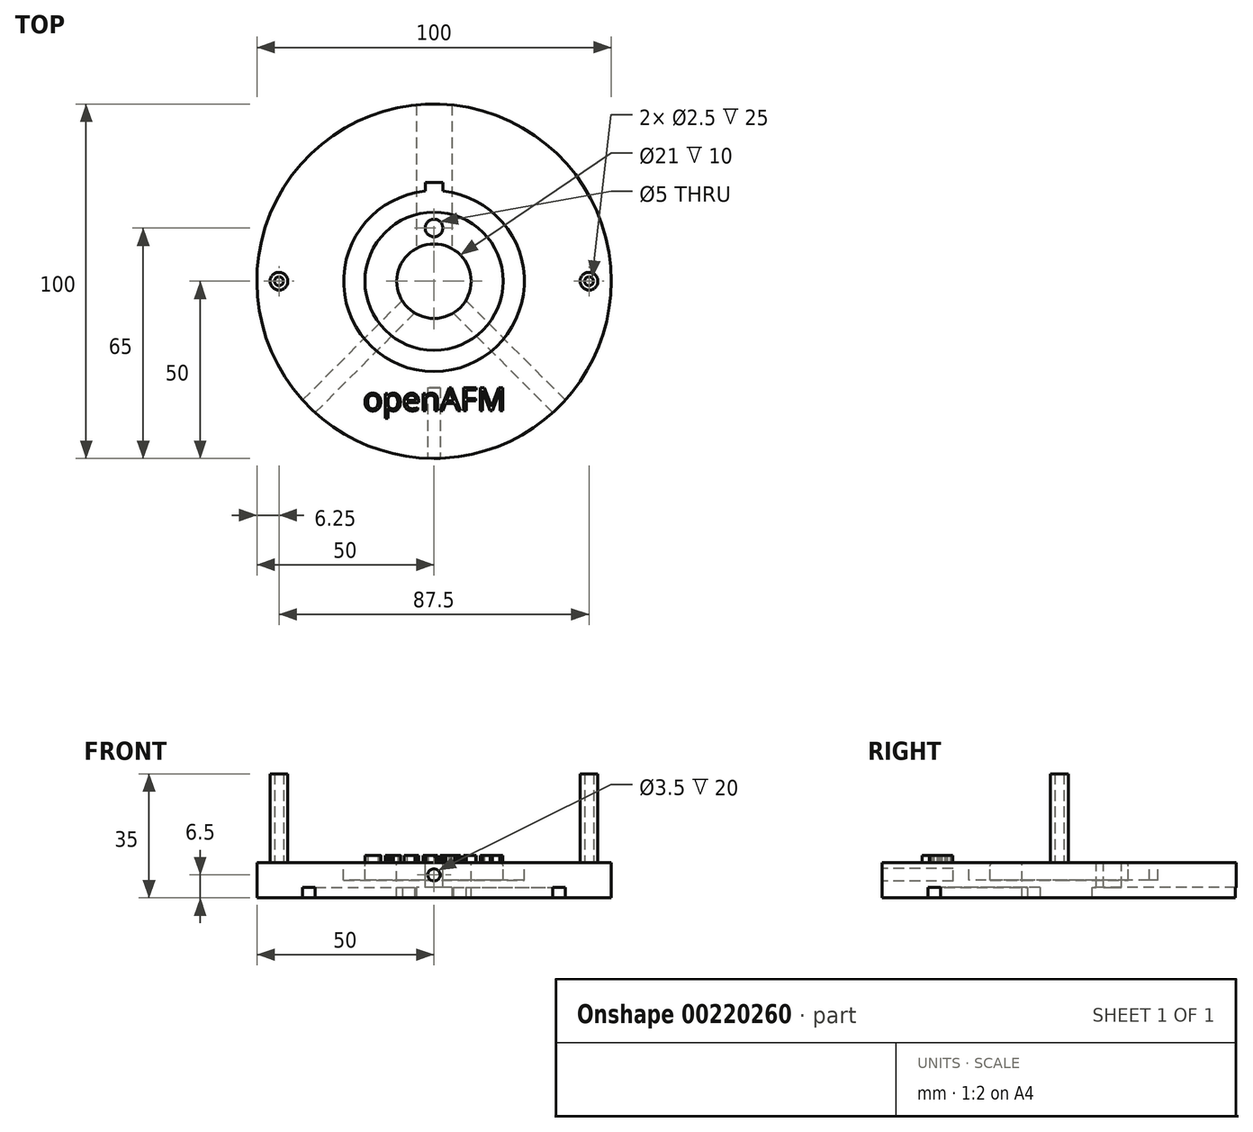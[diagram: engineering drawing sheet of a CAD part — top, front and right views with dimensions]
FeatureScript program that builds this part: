
annotation { "Feature Type Name" : "Feature", "Feature Type Description" : "" }
export const myFeature = defineFeature(function(context is Context, id is Id, definition is map)
    precondition{}
    {
        {
            var Q0;
            Q0=qCreatedBy(makeId("Top.planeOp"),FACE);
            var sketch = newSketch(context, id + "F0", { "sketchPlane" : qUnion([Q0])});
            skCircle(sketch, "E0", {"center": v(0, 0) * mm, "radius": 50 * mm});
            skSolve(sketch);
        }
        {
            var Q0;
            Q0=makeQuery(id+"F0.imprint","IMPRINT",FACE,{"disambiguationData":[TD([[makeQuery(id+"F0.imprint","IMPRINT",EDGE,{"derivedFrom":sQuery(id+"F0.wireOp",EDGE,"E0")}),1.0]])]});
            extrude(context, id + "F1", {"entities" : qUnion([Q0]), "depth" : 10 * mm});
        }
        {
            var Q0;
            Q0=makeQuery(id+"F1.opExtrude","CAP_FACE",FACE,{"disambiguationData":[OSD([sQuery(id+"F0.wireOp",EDGE,"E0")])],"isStart":false});
            var sketch = newSketch(context, id + "F2", { "sketchPlane" : qUnion([Q0])});
            skCircle(sketch, "E1", {"center": v(0, 0) * mm, "radius": 10.5 * mm});
            skSolve(sketch);
        }
        {
            var Q0;
            Q0=makeQuery(id+"F2.imprint","IMPRINT",FACE,{"disambiguationData":[TD([[makeQuery(id+"F2.imprint","IMPRINT",EDGE,{"derivedFrom":sQuery(id+"F2.wireOp",EDGE,"E1")}),1.0]])]});
            extrude(context, id + "F3", {"entities" : qUnion([Q0]), "operationType" : NewBodyOperationType.REMOVE, "oppositeDirection" : true, "depth" : 10 * mm});
        }
        {
            var Q0;
            Q0=makeQuery(id+"F1.opExtrude","CAP_FACE",FACE,{"disambiguationData":[OSD([sQuery(id+"F0.wireOp",EDGE,"E0")])],"isStart":true});
            var sketch = newSketch(context, id + "F4", { "sketchPlane" : qUnion([Q0])});
            skLineSegment(sketch, "E2", {"start": v(0, 0) * mm, "end": v(50, 0) * mm, "construction": true});
            skLineSegment(sketch, "E3", {"start": v(0, 0) * mm, "end": v(0, 50) * mm, "construction": true});
            skLineSegment(sketch, "E4", {"start": v(0, 0) * mm, "end": v(-50, 0) * mm, "construction": true});
            skLineSegment(sketch, "E5", {"start": v(0, 0) * mm, "end": v(0, -50) * mm, "construction": true});
            skLineSegment(sketch, "E6", {"start": v(0, 0) * mm, "end": v(-35.36, 35.36) * mm, "construction": true});
            skLineSegment(sketch, "E7", {"start": v(0, 0) * mm, "end": v(35.36, -35.36) * mm, "construction": true});
            skLineSegment(sketch, "E8", {"start": v(0, 0) * mm, "end": v(35.36, 35.36) * mm, "construction": true});
            skLineSegment(sketch, "E9", {"start": v(0, 0) * mm, "end": v(-35.36, -35.36) * mm, "construction": true});
            skLineSegment(sketch, "E10", {"start": v(-37.08, 33.54) * mm, "end": v(-8.98, 5.44) * mm});
            skLineSegment(sketch, "E11", {"start": v(-33.54, 37.08) * mm, "end": v(-5.44, 8.98) * mm});
            skArc(sketch, "E12", {"start": v(-8.98, -5.44) * mm, "mid": v(-7.42, -7.42) * mm, "end": v(-5.44, -8.98) * mm});
            skLineSegment(sketch, "E13.trimOffspring", {"start": v(5.44, -8.98) * mm, "end": v(33.54, -37.08) * mm});
            skLineSegment(sketch, "E14.trimOffspring", {"start": v(8.98, -5.44) * mm, "end": v(37.08, -33.54) * mm});
            skArc(sketch, "E15", {"start": v(-37.08, -33.54) * mm, "mid": v(-35.36, -35.36) * mm, "end": v(-33.54, -37.08) * mm});
            skLineSegment(sketch, "E16", {"start": v(-37.08, -33.54) * mm, "end": v(-8.98, -5.44) * mm});
            skLineSegment(sketch, "E17", {"start": v(-33.54, -37.08) * mm, "end": v(-5.44, -8.98) * mm});
            skLineSegment(sketch, "E18.trimOffspring", {"start": v(5.44, 8.98) * mm, "end": v(33.54, 37.08) * mm});
            skLineSegment(sketch, "E19.trimOffspring", {"start": v(8.98, 5.44) * mm, "end": v(37.08, 33.54) * mm});
            skArc(sketch, "E20.trimOffspring", {"start": v(-33.54, 37.08) * mm, "mid": v(-35.36, 35.36) * mm, "end": v(-37.08, 33.54) * mm});
            skArc(sketch, "E21.trimOffspring", {"start": v(37.08, 33.54) * mm, "mid": v(35.36, 35.36) * mm, "end": v(33.54, 37.08) * mm});
            skArc(sketch, "E22.trimOffspring", {"start": v(33.54, -37.08) * mm, "mid": v(35.36, -35.36) * mm, "end": v(37.08, -33.54) * mm});
            skArc(sketch, "E23.trimOffspring", {"start": v(-5.44, 8.98) * mm, "mid": v(-7.42, 7.42) * mm, "end": v(-8.98, 5.44) * mm});
            skArc(sketch, "E24.trimOffspring", {"start": v(8.98, 5.44) * mm, "mid": v(7.42, 7.42) * mm, "end": v(5.44, 8.98) * mm});
            skArc(sketch, "E25.trimOffspring", {"start": v(5.44, -8.98) * mm, "mid": v(7.42, -7.42) * mm, "end": v(8.98, -5.44) * mm});
            skLineSegment(sketch, "E26", {"start": v(-2.5, 10.2) * mm, "end": v(-2.5, 49.94) * mm});
            skLineSegment(sketch, "E27", {"start": v(2.5, 10.2) * mm, "end": v(2.5, 49.94) * mm});
            skLineSegment(sketch, "E28", {"start": v(2.5, 49.94) * mm, "end": v(2.93, 49.2) * mm});
            skArc(sketch, "E29", {"start": v(-2.5, 10.2) * mm, "mid": v(0, 10.5) * mm, "end": v(2.5, 10.2) * mm});
            skArc(sketch, "E30", {"start": v(-2.5, 49.94) * mm, "mid": v(0, 50) * mm, "end": v(2.5, 49.94) * mm});
            skSolve(sketch);
        }
        {
            var Q0;
            Q0=makeQuery(id+"F4.imprint","IMPRINT",FACE,{"disambiguationData":[TD([[makeQuery(id+"F4.imprint","IMPRINT",EDGE,{"derivedFrom":sQuery(id+"F4.wireOp",EDGE,"E10")}),1.0]])]});
            var Q1;
            Q1=makeQuery(id+"F4.imprint","IMPRINT",FACE,{"disambiguationData":[TD([[makeQuery(id+"F4.imprint","IMPRINT",EDGE,{"derivedFrom":sQuery(id+"F4.wireOp",EDGE,"E18.trimOffspring")}),-1.0]])]});
            extrude(context, id + "F5", {"entities" : qUnion([Q0, Q1]), "operationType" : NewBodyOperationType.REMOVE, "oppositeDirection" : true, "depth" : 3 * mm});
        }
        {
            var Q0;
            Q0=makeQuery(id+"F1.opExtrude","CAP_FACE",FACE,{"disambiguationData":[OSD([sQuery(id+"F0.wireOp",EDGE,"E0")])],"isStart":false});
            var sketch = newSketch(context, id + "F6", { "sketchPlane" : qUnion([Q0])});
            skCircle(sketch, "E31", {"center": v(0, 0) * mm, "radius": 19.5 * mm});
            skCircle(sketch, "E32", {"center": v(0, 0) * mm, "radius": 25.5 * mm});
            skSolve(sketch);
        }
        {
            var Q0;
            Q0=makeQuery(id+"F6.imprint","IMPRINT",FACE,{"disambiguationData":[TD([[makeQuery(id+"F6.imprint","IMPRINT",EDGE,{"derivedFrom":sQuery(id+"F6.wireOp",EDGE,"E31")}),-1.0]])]});
            extrude(context, id + "F7", {"entities" : qUnion([Q0]), "operationType" : NewBodyOperationType.REMOVE, "oppositeDirection" : true, "depth" : 5 * mm});
        }
        {
            var Q0;
            {var subQ0=sQuery(id+"F0.wireOp",EDGE,"E0");Q0=makeQuery(id+"F7.boolean.opBoolean","SPLIT",FACE,{"disambiguationData":[TD([makeQuery(id+"F1.opExtrude","SWEPT_FACE",FACE,{"disambiguationData":[OSD([subQ0])]})])],"derivedFrom":makeQuery(id+"F1.opExtrude","CAP_FACE",FACE,{"disambiguationData":[OSD([subQ0])],"isStart":false})});}
            var sketch = newSketch(context, id + "F8", { "sketchPlane" : qUnion([Q0])});
            skCircle(sketch, "E33", {"center": v(-43.75, 0) * mm, "radius": 2.5 * mm});
            skCircle(sketch, "E34", {"center": v(-43.75, 0) * mm, "radius": 1.25 * mm});
            skCircle(sketch, "E35", {"center": v(43.75, 0) * mm, "radius": 2.5 * mm});
            skCircle(sketch, "E36", {"center": v(43.75, 0) * mm, "radius": 1.25 * mm});
            skSolve(sketch);
        }
        {
            var Q0;
            Q0=qSketchRegion(id+"F8",true);
            extrude(context, id + "F9", {"entities" : qUnion([Q0]), "operationType" : NewBodyOperationType.ADD, "depth" : 25 * mm});
        }
        {
            var Q0;
            Q0=makeQuery(id+"F7.boolean.opBoolean","COPY",EDGE,{"derivedFrom":makeQuery(id+"F7.opExtrude","CAP_EDGE",EDGE,{"disambiguationData":[OSD([sQuery(id+"F6.wireOp",EDGE,"E31")])],"isStart":true})});
            var Q1;
            Q1=makeQuery(id+"F7.boolean.opBoolean","COPY",EDGE,{"derivedFrom":makeQuery(id+"F7.opExtrude","CAP_EDGE",EDGE,{"disambiguationData":[OSD([sQuery(id+"F6.wireOp",EDGE,"E32")])],"isStart":true})});
            fillet(context, id + "F10", {"entities" : qUnion([Q0, Q1]), "radius" : 1 * mm, "tangentPropagation" : true, "allowEdgeOverflow" : false});
        }
        {
            var Q0;
            Q0=makeQuery(id+"F7.boolean.opBoolean","SPLIT",FACE,{"disambiguationData":[TD([makeQuery(id+"F3.boolean.opBoolean","COPY",FACE,{"derivedFrom":makeQuery(id+"F3.opExtrude","SWEPT_FACE",FACE,{"disambiguationData":[OSD([sQuery(id+"F2.wireOp",EDGE,"E1")])]})})])],"derivedFrom":makeQuery(id+"F1.opExtrude","CAP_FACE",FACE,{"disambiguationData":[OSD([sQuery(id+"F0.wireOp",EDGE,"E0")])],"isStart":false})});
            var sketch = newSketch(context, id + "F11", { "sketchPlane" : qUnion([Q0])});
            skCircle(sketch, "E37", {"center": v(0, 15) * mm, "radius": 2.5 * mm});
            skSolve(sketch);
        }
        {
            var Q0;
            Q0=qSketchRegion(id+"F11",true);
            extrude(context, id + "F12", {"entities" : qUnion([Q0]), "operationType" : NewBodyOperationType.REMOVE, "oppositeDirection" : true, "depth" : 10 * mm});
        }
        {
            var Q0;
            Q0=qCreatedBy(makeId("Front.planeOp"),FACE);
            var sketch = newSketch(context, id + "F13", { "sketchPlane" : qUnion([Q0])});
            skLineSegment(sketch, "E38", {"start": v(-5, 3) * mm, "end": v(-5, 0) * mm});
            skLineSegment(sketch, "E39", {"start": v(-5, 0) * mm, "end": v(5, 0) * mm});
            skLineSegment(sketch, "E40", {"start": v(5, 0) * mm, "end": v(5, 3) * mm});
            skLineSegment(sketch, "E41", {"start": v(5, 3) * mm, "end": v(-5, 3) * mm});
            skSolve(sketch);
        }
        {
            var Q0;
            Q0=qSketchRegion(id+"F13",true);
            extrude(context, id + "F14", {"entities" : qUnion([Q0]), "operationType" : NewBodyOperationType.REMOVE, "oppositeDirection" : true, "depth" : 50 * mm});
        }
        {
            var Q0;
            {var subQ0=sQuery(id+"F0.wireOp",EDGE,"E0");var subQ1=makeQuery(id+"F1.opExtrude","SWEPT_FACE",FACE,{"disambiguationData":[OSD([subQ0])]});Q0=makeQuery(id+"F9.boolean.opBoolean","SPLIT",FACE,{"disambiguationData":[TD([subQ1])],"derivedFrom":makeQuery(id+"F7.boolean.opBoolean","SPLIT",FACE,{"disambiguationData":[TD([subQ1])],"derivedFrom":makeQuery(id+"F1.opExtrude","CAP_FACE",FACE,{"disambiguationData":[OSD([subQ0])],"isStart":false})})});}
            var sketch = newSketch(context, id + "F15", { "sketchPlane" : qUnion([Q0])});
            skArc(sketch, "E42", {"start": v(2.5, 25.38) * mm, "mid": v(0, 25.5) * mm, "end": v(-2.5, 25.38) * mm});
            skLineSegment(sketch, "E43", {"start": v(0, 0) * mm, "end": v(0, 32.13) * mm, "construction": true});
            skLineSegment(sketch, "E44", {"start": v(-2.5, 25.38) * mm, "end": v(-2.5, 27.88) * mm});
            skLineSegment(sketch, "E45", {"start": v(-2.5, 27.88) * mm, "end": v(2.5, 27.88) * mm});
            skLineSegment(sketch, "E46", {"start": v(2.5, 27.88) * mm, "end": v(2.5, 25.38) * mm});
            skSolve(sketch);
        }
        {
            var Q0;
            Q0=qSketchRegion(id+"F15",true);
            extrude(context, id + "F16", {"entities" : qUnion([Q0]), "operationType" : NewBodyOperationType.REMOVE, "oppositeDirection" : true, "depth" : 5 * mm});
        }
        {
            var Q0;
            {var subQ0=sQuery(id+"F0.wireOp",EDGE,"E0");var subQ1=makeQuery(id+"F1.opExtrude","SWEPT_FACE",FACE,{"disambiguationData":[OSD([subQ0])]});Q0=makeQuery(id+"F9.boolean.opBoolean","SPLIT",FACE,{"disambiguationData":[TD([subQ1])],"derivedFrom":makeQuery(id+"F7.boolean.opBoolean","SPLIT",FACE,{"disambiguationData":[TD([subQ1])],"derivedFrom":makeQuery(id+"F1.opExtrude","CAP_FACE",FACE,{"disambiguationData":[OSD([subQ0])],"isStart":false})})});}
            var sketch = newSketch(context, id + "F17", { "sketchPlane" : qUnion([Q0])});
            skText(sketch, "E47", { "text": "openAFM\n", "fontName": "OpenSans-Regular.ttf"});
            const initialGuessF17  = {"E47": [-0.02, -0.03653, 1, 0, 0.00653]};
            skSetInitialGuess(sketch, initialGuessF17);
            skSolve(sketch);
        }
        {
            var Q0;
            Q0=qSketchRegion(id+"F17",true);
            extrude(context, id + "F18", {"entities" : qUnion([Q0]), "operationType" : NewBodyOperationType.ADD, "depth" : 2 * mm});
        }
        {
            var Q0;
            Q0=qCreatedBy(makeId("Front.planeOp"),FACE);
            cPlane(context, id + "F19", {"entities" : qUnion([Q0]), "cplaneType" : CPlaneType.OFFSET, "offset" : 50 * mm, "width" : 150 * mm, "height" : 150 * mm});
        }
        {
            var Q0;
            Q0=qCreatedBy(makeId("Front.planeOp"),FACE);
            cPlane(context, id + "F20", {"entities" : qUnion([Q0]), "cplaneType" : CPlaneType.OFFSET, "offset" : 50 * mm, "oppositeDirection" : true, "width" : 150 * mm, "height" : 150 * mm});
        }
        {
            var Q0;
            Q0=qCreatedBy(makeId("Right.planeOp"),FACE);
            cPlane(context, id + "F21", {"entities" : qUnion([Q0]), "cplaneType" : CPlaneType.OFFSET, "offset" : 50 * mm, "width" : 150 * mm, "height" : 150 * mm});
        }
        {
            var Q0;
            Q0=qCreatedBy(makeId("Right.planeOp"),FACE);
            cPlane(context, id + "F22", {"entities" : qUnion([Q0]), "cplaneType" : CPlaneType.OFFSET, "offset" : 50 * mm, "oppositeDirection" : true, "width" : 150 * mm, "height" : 150 * mm});
        }
        {
            var Q0;
            Q0=qCreatedBy(id+"F19.planeOp",FACE);
            var sketch = newSketch(context, id + "F23", { "sketchPlane" : qUnion([Q0])});
            skCircle(sketch, "E48", {"center": v(0, 6.5) * mm, "radius": 1.75 * mm});
            skSolve(sketch);
        }
        {
            var Q0;
            Q0=makeQuery(id+"F23.imprint","IMPRINT",FACE,{"disambiguationData":[TD([[makeQuery(id+"F23.imprint","IMPRINT",EDGE,{"derivedFrom":sQuery(id+"F23.wireOp",EDGE,"E48")}),1.0]])]});
            extrude(context, id + "F24", {"entities" : qUnion([Q0]), "operationType" : NewBodyOperationType.REMOVE, "oppositeDirection" : true, "depth" : 20 * mm});
        }
        {
            var Q0;
            Q0=qCreatedBy(makeId("Right.planeOp"),FACE);
            var sketch = newSketch(context, id + "F25", { "sketchPlane" : qUnion([Q0])});
            skLineSegment(sketch, "E49", {"start": v(0, 60) * mm, "end": v(0, 0) * mm});
            skSolve(sketch);
        }
    });
